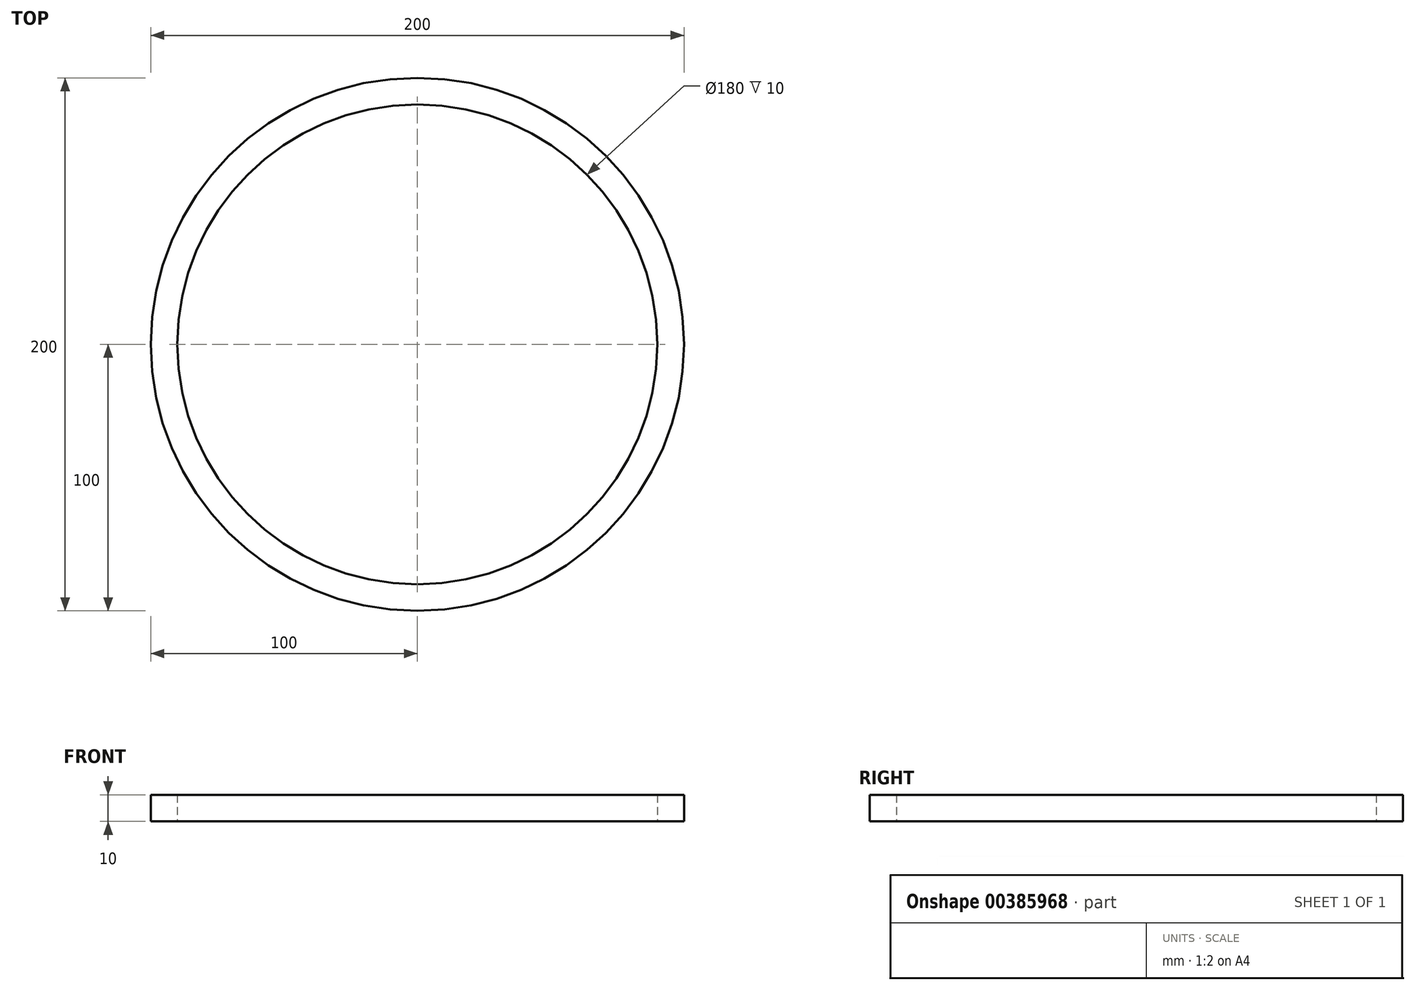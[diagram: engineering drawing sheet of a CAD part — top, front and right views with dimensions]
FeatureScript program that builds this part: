
annotation { "Feature Type Name" : "Feature", "Feature Type Description" : "" }
export const myFeature = defineFeature(function(context is Context, id is Id, definition is map)
    precondition{}
    {
        {
            var Q0;
            Q0=qCreatedBy(makeId("Top.planeOp"),FACE);
            var sketch = newSketch(context, id + "F0", { "sketchPlane" : qUnion([Q0])});
            skCircle(sketch, "E0", {"center": v(0, 0) * mm, "radius": 100 * mm});
            skCircle(sketch, "E1", {"center": v(0, 0) * mm, "radius": 90 * mm});
            skSolve(sketch);
        }
        {
            var Q0;
            Q0=makeQuery(id+"F0.imprint","IMPRINT",FACE,{"disambiguationData":[TD([[makeQuery(id+"F0.imprint","IMPRINT",EDGE,{"derivedFrom":sQuery(id+"F0.wireOp",EDGE,"E0")}),1.0]])]});
            var Q1;
            Q1 = qSketchRegion(id + "F2", true);
            extrude(context, id + "F1", {"entities" : qUnion([Q0, Q1]), "depth" : 10 * mm});
        }
    });
